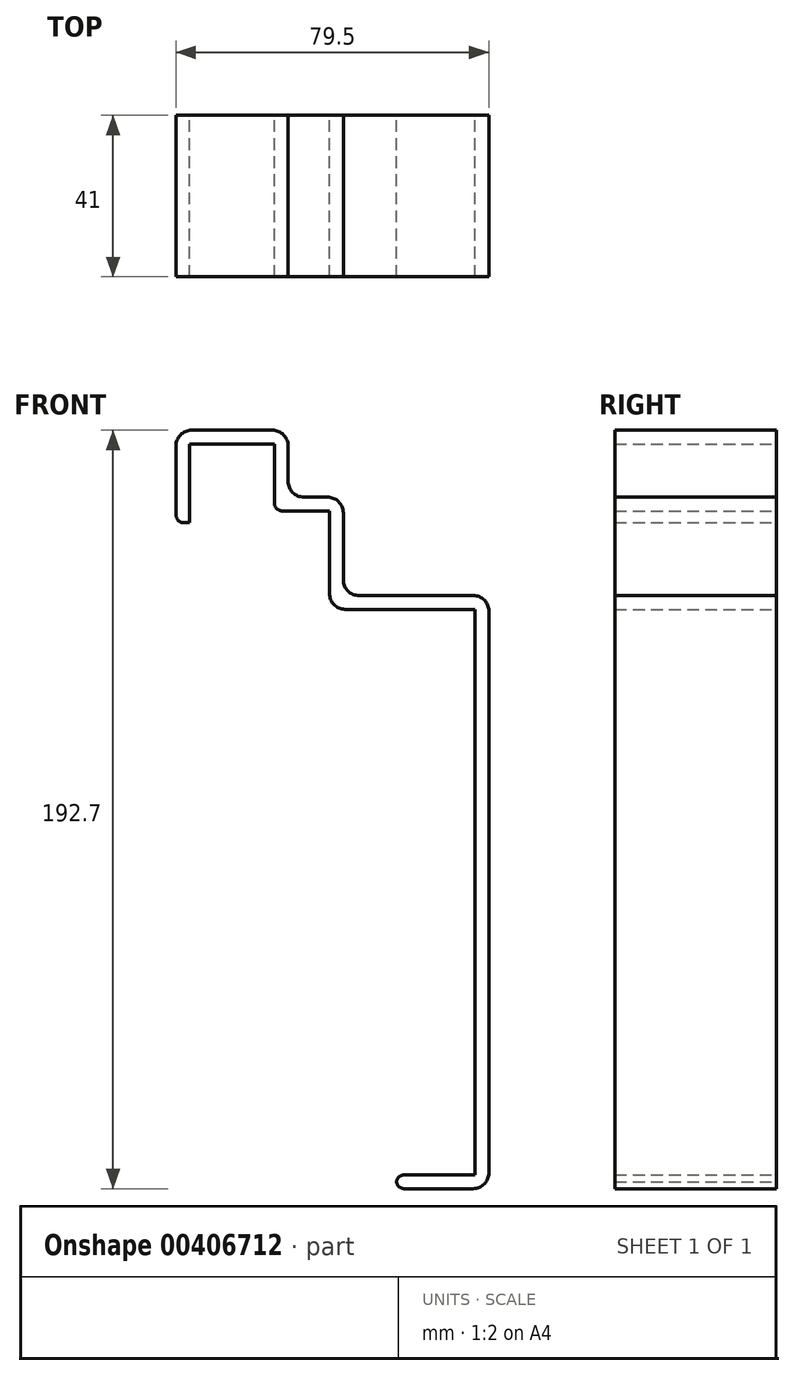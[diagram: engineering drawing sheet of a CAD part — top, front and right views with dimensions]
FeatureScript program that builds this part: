
annotation { "Feature Type Name" : "Feature", "Feature Type Description" : "" }
export const myFeature = defineFeature(function(context is Context, id is Id, definition is map)
    precondition{}
    {
        {
            var Q0;
            Q0=qCreatedBy(makeId("Front.planeOp"),FACE);
            var sketch = newSketch(context, id + "F0", { "sketchPlane" : qUnion([Q0])});
            skLineSegment(sketch, "E0", {"start": v(-39, 18.5) * mm, "end": v(-39, 38.5) * mm});
            skLineSegment(sketch, "E1", {"start": v(-39, 38.5) * mm, "end": v(-17.5, 38.5) * mm});
            skLineSegment(sketch, "E2", {"start": v(-17.5, 38.5) * mm, "end": v(-17.5, 21.5) * mm});
            skLineSegment(sketch, "E3", {"start": v(-17.5, 21.5) * mm, "end": v(-3.5, 21.5) * mm});
            skLineSegment(sketch, "E4", {"start": v(-3.5, 21.5) * mm, "end": v(-3.5, -3.5) * mm});
            skLineSegment(sketch, "E5", {"start": v(-3.5, -3.5) * mm, "end": v(33.5, -3.5) * mm});
            skLineSegment(sketch, "E6", {"start": v(33.5, -3.5) * mm, "end": v(33.5, -147.2) * mm});
            skLineSegment(sketch, "E7", {"start": v(33.5, -147.2) * mm, "end": v(13.5, -147.2) * mm});
            skLineSegment(sketch, "E8.0", {"start": v(37, -150.7) * mm, "end": v(13.5, -150.7) * mm});
            skLineSegment(sketch, "E8.1", {"start": v(37, 0) * mm, "end": v(37, -150.7) * mm});
            skLineSegment(sketch, "E8.2", {"start": v(0, 0) * mm, "end": v(37, 0) * mm});
            skLineSegment(sketch, "E8.3", {"start": v(0, 25) * mm, "end": v(0, 0) * mm});
            skLineSegment(sketch, "E8.4", {"start": v(-42.5, 18.5) * mm, "end": v(-42.5, 42) * mm});
            skLineSegment(sketch, "E8.5", {"start": v(-42.5, 42) * mm, "end": v(-14, 42) * mm});
            skLineSegment(sketch, "E8.6", {"start": v(-14, 42) * mm, "end": v(-14, 25) * mm});
            skLineSegment(sketch, "E8.7", {"start": v(-14, 25) * mm, "end": v(0, 25) * mm});
            skLineSegment(sketch, "E9", {"start": v(-42.5, 18.5) * mm, "end": v(-39, 18.5) * mm});
            skLineSegment(sketch, "E10", {"start": v(13.5, -147.2) * mm, "end": v(13.5, -150.7) * mm});
            skLineSegment(sketch, "E11", {"start": v(0, 0) * mm, "end": v(0, -3.5) * mm});
            skSolve(sketch);
        }
        {
            var Q0;
            Q0=makeQuery(id+"F0.imprint","IMPRINT",FACE,{"disambiguationData":[TD([[makeQuery(id+"F0.imprint","IMPRINT",EDGE,{"derivedFrom":sQuery(id+"F0.wireOp",EDGE,"E0")}),1.0]])]});
            var Q1;
            {var subQ1=sQuery(id+"F0.wireOp",EDGE,"E6");Q1=makeQuery(id+"F0.imprint","IMPRINT",FACE,{"disambiguationData":[TD([[makeQuery(id+"F0.imprint","IMPRINT",EDGE,{"derivedFrom":subQ1}),1.0]])]});}
            extrude(context, id + "F1", {"entities" : qUnion([Q0, Q1]), "depth" : 41 * mm});
        }
        {
            var Q0;
            Q0=makeQuery(id+"F1.opExtrude","SWEPT_EDGE",EDGE,{"disambiguationData":[OSD([sQuery(id+"F0.wireOp",EDGE,"E8.4"),sQuery(id+"F0.wireOp",EDGE,"E8.5")])]});
            var Q1;
            Q1=makeQuery(id+"F1.opExtrude","SWEPT_EDGE",EDGE,{"disambiguationData":[OSD([sQuery(id+"F0.wireOp",EDGE,"E8.5"),sQuery(id+"F0.wireOp",EDGE,"E8.6")])]});
            var Q2;
            Q2=makeQuery(id+"F1.opExtrude","SWEPT_EDGE",EDGE,{"disambiguationData":[OSD([sQuery(id+"F0.wireOp",EDGE,"E8.3"),sQuery(id+"F0.wireOp",EDGE,"E8.7")])]});
            var Q3;
            Q3=makeQuery(id+"F1.opExtrude","SWEPT_EDGE",EDGE,{"disambiguationData":[OSD([sQuery(id+"F0.wireOp",EDGE,"E8.2"),sQuery(id+"F0.wireOp",EDGE,"E8.3"),sQuery(id+"F0.wireOp",EDGE,"E11")])]});
            var Q4;
            Q4=makeQuery(id+"F1.opExtrude","SWEPT_EDGE",EDGE,{"disambiguationData":[OSD([sQuery(id+"F0.wireOp",EDGE,"E8.6"),sQuery(id+"F0.wireOp",EDGE,"E8.7")])]});
            var Q5;
            Q5=makeQuery(id+"F1.opExtrude","SWEPT_EDGE",EDGE,{"disambiguationData":[OSD([sQuery(id+"F0.wireOp",EDGE,"E8.1"),sQuery(id+"F0.wireOp",EDGE,"E8.2")])]});
            var Q6;
            Q6=makeQuery(id+"F1.opExtrude","SWEPT_EDGE",EDGE,{"disambiguationData":[OSD([sQuery(id+"F0.wireOp",EDGE,"E8.0"),sQuery(id+"F0.wireOp",EDGE,"E8.1")])]});
            var Q7;
            Q7=makeQuery(id+"F1.opExtrude","SWEPT_EDGE",EDGE,{"disambiguationData":[OSD([sQuery(id+"F0.wireOp",EDGE,"E4"),sQuery(id+"F0.wireOp",EDGE,"E5")])]});
            fillet(context, id + "F2", {"entities" : qUnion([Q0, Q1, Q2, Q3, Q4, Q5, Q6, Q7]), "radius" : 4 * mm, "tangentPropagation" : true, "allowEdgeOverflow" : false});
        }
        {
            var Q0;
            Q0=makeQuery(id+"F1.opExtrude","SWEPT_EDGE",EDGE,{"disambiguationData":[OSD([sQuery(id+"F0.wireOp",EDGE,"E8.4"),sQuery(id+"F0.wireOp",EDGE,"E9")])]});
            var Q1;
            Q1=makeQuery(id+"F1.opExtrude","SWEPT_EDGE",EDGE,{"disambiguationData":[OSD([sQuery(id+"F0.wireOp",EDGE,"E7"),sQuery(id+"F0.wireOp",EDGE,"E10")])]});
            var Q2;
            Q2=makeQuery(id+"F1.opExtrude","SWEPT_EDGE",EDGE,{"disambiguationData":[OSD([sQuery(id+"F0.wireOp",EDGE,"E8.0"),sQuery(id+"F0.wireOp",EDGE,"E10")])]});
            var Q3;
            Q3=makeQuery(id+"F1.opExtrude","SWEPT_EDGE",EDGE,{"disambiguationData":[OSD([sQuery(id+"F0.wireOp",EDGE,"E2"),sQuery(id+"F0.wireOp",EDGE,"E3")])]});
            fillet(context, id + "F3", {"entities" : qUnion([Q0, Q1, Q2, Q3]), "radius" : 2 * mm, "tangentPropagation" : true, "allowEdgeOverflow" : false});
        }
    });
